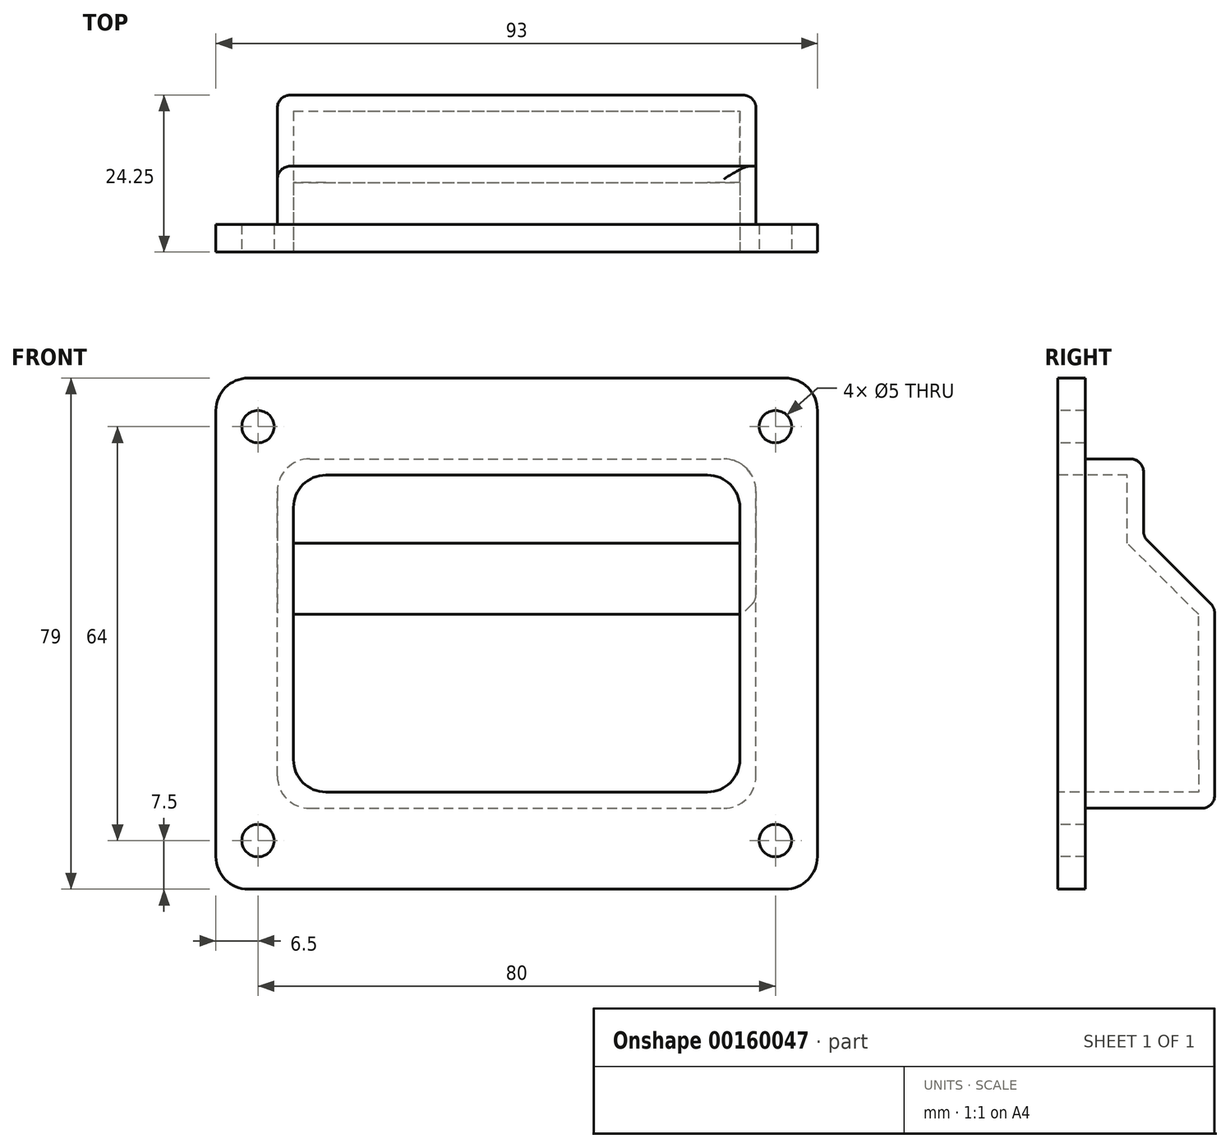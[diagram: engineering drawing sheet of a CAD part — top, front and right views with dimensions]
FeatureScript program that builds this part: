
annotation { "Feature Type Name" : "Feature", "Feature Type Description" : "" }
export const myFeature = defineFeature(function(context is Context, id is Id, definition is map)
    precondition{}
    {
        {
            var Q0;
            Q0=qCreatedBy(makeId("Front.planeOp"),FACE);
            var sketch = newSketch(context, id + "F0", { "sketchPlane" : qUnion([Q0])});
            skLineSegment(sketch, "E0.bottom", {"start": v(46.5, -39.5) * mm, "end": v(-46.5, -39.5) * mm});
            skLineSegment(sketch, "E0.top", {"start": v(46.5, 39.5) * mm, "end": v(-46.5, 39.5) * mm});
            skLineSegment(sketch, "E0.left", {"start": v(46.5, -39.5) * mm, "end": v(46.5, 39.5) * mm});
            skLineSegment(sketch, "E0.right", {"start": v(-46.5, -39.5) * mm, "end": v(-46.5, 39.5) * mm});
            skPoint(sketch, "E0.middle", {"position": v(0, 0) * mm});
            skLineSegment(sketch, "E1.bottom", {"start": v(34.5, -24.5) * mm, "end": v(-34.5, -24.5) * mm});
            skLineSegment(sketch, "E1.top", {"start": v(34.5, 24.5) * mm, "end": v(-34.5, 24.5) * mm});
            skLineSegment(sketch, "E1.left", {"start": v(34.5, -24.5) * mm, "end": v(34.5, 24.5) * mm});
            skLineSegment(sketch, "E1.right", {"start": v(-34.5, -24.5) * mm, "end": v(-34.5, 24.5) * mm});
            skCircle(sketch, "E2", {"center": v(40, 32) * mm, "radius": 2.5 * mm});
            skCircle(sketch, "E3.MirrorC", {"center": v(40, -32) * mm, "radius": 2.5 * mm});
            skCircle(sketch, "E4.MirrorC", {"center": v(-40, 32) * mm, "radius": 2.5 * mm});
            skCircle(sketch, "E5.MirrorC", {"center": v(-40, -32) * mm, "radius": 2.5 * mm});
            skSolve(sketch);
        }
        {
            var Q0;
            Q0=makeQuery(id+"F0.imprint","IMPRINT",FACE,{"disambiguationData":[TD([[makeQuery(id+"F0.imprint","IMPRINT",EDGE,{"derivedFrom":sQuery(id+"F0.wireOp",EDGE,"E0.bottom")}),-1.0]])]});
            extrude(context, id + "F1", {"entities" : qUnion([Q0]), "oppositeDirection" : true, "depth" : 4.25 * mm});
        }
        {
            var Q0;
            Q0=makeQuery(id+"F1.opExtrude","CAP_FACE",FACE,{"disambiguationData":[OSD([sQuery(id+"F0.wireOp",EDGE,"E0.bottom"),sQuery(id+"F0.wireOp",EDGE,"E0.top"),sQuery(id+"F0.wireOp",EDGE,"E0.left"),sQuery(id+"F0.wireOp",EDGE,"E0.right"),sQuery(id+"F0.wireOp",EDGE,"E1.bottom"),sQuery(id+"F0.wireOp",EDGE,"E1.top"),sQuery(id+"F0.wireOp",EDGE,"E1.left"),sQuery(id+"F0.wireOp",EDGE,"E1.right"),sQuery(id+"F0.wireOp",EDGE,"E2"),sQuery(id+"F0.wireOp",EDGE,"E3.MirrorC"),sQuery(id+"F0.wireOp",EDGE,"E4.MirrorC"),sQuery(id+"F0.wireOp",EDGE,"E5.MirrorC")])],"isStart":false});
            var sketch = newSketch(context, id + "F2", { "sketchPlane" : qUnion([Q0])});
            skLineSegment(sketch, "E6.bottom", {"start": v(37, -27) * mm, "end": v(-37, -27) * mm});
            skLineSegment(sketch, "E6.top", {"start": v(37, 27) * mm, "end": v(-37, 27) * mm});
            skLineSegment(sketch, "E6.left", {"start": v(37, -27) * mm, "end": v(37, 27) * mm});
            skLineSegment(sketch, "E6.right", {"start": v(-37, -27) * mm, "end": v(-37, 27) * mm});
            skPoint(sketch, "E6.middle", {"position": v(0, 0) * mm});
            skLineSegment(sketch, "E7.bottom", {"start": v(34.5, -24.5) * mm, "end": v(-34.5, -24.5) * mm});
            skLineSegment(sketch, "E7.top", {"start": v(34.5, 24.5) * mm, "end": v(-34.5, 24.5) * mm});
            skLineSegment(sketch, "E7.left", {"start": v(34.5, -24.5) * mm, "end": v(34.5, 24.5) * mm});
            skLineSegment(sketch, "E7.right", {"start": v(-34.5, -24.5) * mm, "end": v(-34.5, 24.5) * mm});
            skSolve(sketch);
        }
        {
            var Q0;
            Q0 = qSketchRegion(id + "F2", true);
            extrude(context, id + "F3", {"entities" : qUnion([Q0]), "operationType" : NewBodyOperationType.ADD, "depth" : 20 * mm});
        }
        {
            var Q0;
            Q0=makeQuery(id+"F3.opExtrude","CAP_FACE",FACE,{"disambiguationData":[OSD([sQuery(id+"F2.wireOp",EDGE,"E6.bottom"),sQuery(id+"F2.wireOp",EDGE,"E6.top"),sQuery(id+"F2.wireOp",EDGE,"E6.left"),sQuery(id+"F2.wireOp",EDGE,"E6.right"),sQuery(id+"F2.wireOp",EDGE,"E7.bottom"),sQuery(id+"F2.wireOp",EDGE,"E7.top"),sQuery(id+"F2.wireOp",EDGE,"E7.left"),sQuery(id+"F2.wireOp",EDGE,"E7.right")])],"isStart":false});
            var sketch = newSketch(context, id + "F4", { "sketchPlane" : qUnion([Q0])});
            skLineSegment(sketch, "E8.bottom", {"start": v(37, -27) * mm, "end": v(-37, -27) * mm});
            skLineSegment(sketch, "E8.top", {"start": v(37, 27) * mm, "end": v(-37, 27) * mm});
            skLineSegment(sketch, "E8.left", {"start": v(37, -27) * mm, "end": v(37, 27) * mm});
            skLineSegment(sketch, "E8.right", {"start": v(-37, -27) * mm, "end": v(-37, 27) * mm});
            skPoint(sketch, "E8.middle", {"position": v(0, 0) * mm});
            skSolve(sketch);
        }
        {
            var Q0;
            Q0=makeQuery(id+"F3.opExtrude","SWEPT_FACE",FACE,{"disambiguationData":[OSD([sQuery(id+"F2.wireOp",EDGE,"E6.right")])]});
            var sketch = newSketch(context, id + "F5", { "sketchPlane" : qUnion([Q0])});
            skLineSegment(sketch, "E9", {"start": v(13.25, 29.4) * mm, "end": v(13.25, 15) * mm});
            skLineSegment(sketch, "E10", {"start": v(13.25, 15) * mm, "end": v(24.25, 4) * mm});
            skLineSegment(sketch, "E11", {"start": v(24.25, 4) * mm, "end": v(24.25, 29.4) * mm});
            skLineSegment(sketch, "E12", {"start": v(24.25, 29.4) * mm, "end": v(13.25, 29.4) * mm});
            skSolve(sketch);
        }
        {
            var Q0;
            Q0 = qSketchRegion(id + "F5", true);
            extrude(context, id + "F6", {"entities" : qUnion([Q0]), "operationType" : NewBodyOperationType.REMOVE, "endBound" : BoundingType.THROUGH_ALL, "oppositeDirection" : true, "depth" : 25 * mm});
        }
        {
            var Q0;
            Q0=makeQuery(id+"F3.opExtrude","SWEPT_FACE",FACE,{"disambiguationData":[OSD([sQuery(id+"F2.wireOp",EDGE,"E6.right")])]});
            var sketch = newSketch(context, id + "F7", { "sketchPlane" : qUnion([Q0])});
            skLineSegment(sketch, "E13", {"start": v(10.75, 28) * mm, "end": v(10.75, 13.96) * mm});
            skLineSegment(sketch, "E14", {"start": v(10.75, 13.96) * mm, "end": v(21.75, 2.96) * mm});
            skLineSegment(sketch, "E15", {"start": v(21.75, 2.96) * mm, "end": v(21.75, -27) * mm});
            skSolve(sketch);
        }
        {
            var Q0;
            {var subQ2=sQuery(id+"F7.wireOp",EDGE,"E13");Q0=makeQuery(id+"F7.imprint","IMPRINT",FACE,{"disambiguationData":[TD([[makeQuery(id+"F7.imprint","IMPRINT",EDGE,{"derivedFrom":subQ2}),1.0]])]});}
            var Q1;
            Q1=makeQuery(id+"F3.boolean.opBoolean","MERGE",FACE,{"derivedFrom":[makeQuery(id+"F1.opExtrude","SWEPT_FACE",FACE,{"disambiguationData":[OSD([sQuery(id+"F0.wireOp",EDGE,"E1.right")])]}),makeQuery(id+"F3.opExtrude","SWEPT_FACE",FACE,{"disambiguationData":[OSD([sQuery(id+"F2.wireOp",EDGE,"E7.left")])]})]});
            extrude(context, id + "F8", {"entities" : qUnion([Q0]), "operationType" : NewBodyOperationType.ADD, "endBound" : BoundingType.UP_TO_SURFACE, "oppositeDirection" : true, "endBoundEntityFace" : qUnion([Q1]), "depth" : 25 * mm});
        }
        {
            var Q0;
            Q0=makeQuery(id+"F3.opExtrude","SWEPT_EDGE",EDGE,{"disambiguationData":[OSD([sQuery(id+"F2.wireOp",EDGE,"E6.bottom"),sQuery(id+"F2.wireOp",EDGE,"E6.right")])]});
            var Q1;
            Q1=makeQuery(id+"F3.opExtrude","SWEPT_EDGE",EDGE,{"disambiguationData":[OSD([sQuery(id+"F2.wireOp",EDGE,"E6.top"),sQuery(id+"F2.wireOp",EDGE,"E6.right")])]});
            var Q2;
            Q2=makeQuery(id+"F3.opExtrude","SWEPT_EDGE",EDGE,{"disambiguationData":[OSD([sQuery(id+"F2.wireOp",EDGE,"E6.top"),sQuery(id+"F2.wireOp",EDGE,"E6.left")])]});
            var Q3;
            Q3=makeQuery(id+"F3.opExtrude","SWEPT_EDGE",EDGE,{"disambiguationData":[OSD([sQuery(id+"F2.wireOp",EDGE,"E6.bottom"),sQuery(id+"F2.wireOp",EDGE,"E6.left")])]});
            var Q4;
            Q4=makeQuery(id+"F1.opExtrude","SWEPT_EDGE",EDGE,{"disambiguationData":[OSD([sQuery(id+"F0.wireOp",EDGE,"E0.top"),sQuery(id+"F0.wireOp",EDGE,"E0.right")])]});
            var Q5;
            Q5=makeQuery(id+"F1.opExtrude","SWEPT_EDGE",EDGE,{"disambiguationData":[OSD([sQuery(id+"F0.wireOp",EDGE,"E0.bottom"),sQuery(id+"F0.wireOp",EDGE,"E0.right")])]});
            var Q6;
            Q6=makeQuery(id+"F1.opExtrude","SWEPT_EDGE",EDGE,{"disambiguationData":[OSD([sQuery(id+"F0.wireOp",EDGE,"E0.top"),sQuery(id+"F0.wireOp",EDGE,"E0.left")])]});
            var Q7;
            Q7=makeQuery(id+"F1.opExtrude","SWEPT_EDGE",EDGE,{"disambiguationData":[OSD([sQuery(id+"F0.wireOp",EDGE,"E0.bottom"),sQuery(id+"F0.wireOp",EDGE,"E0.left")])]});
            var Q8;
            Q8=makeQuery(id+"F3.boolean.opBoolean","MERGE",EDGE,{"derivedFrom":[makeQuery(id+"F1.opExtrude","SWEPT_EDGE",EDGE,{"disambiguationData":[OSD([sQuery(id+"F0.wireOp",EDGE,"E1.top"),sQuery(id+"F0.wireOp",EDGE,"E1.right")])]}),makeQuery(id+"F3.opExtrude","SWEPT_EDGE",EDGE,{"disambiguationData":[OSD([sQuery(id+"F2.wireOp",EDGE,"E7.top"),sQuery(id+"F2.wireOp",EDGE,"E7.left")])]})]});
            var Q9;
            Q9=makeQuery(id+"F3.boolean.opBoolean","MERGE",EDGE,{"derivedFrom":[makeQuery(id+"F1.opExtrude","SWEPT_EDGE",EDGE,{"disambiguationData":[OSD([sQuery(id+"F0.wireOp",EDGE,"E1.top"),sQuery(id+"F0.wireOp",EDGE,"E1.left")])]}),makeQuery(id+"F3.opExtrude","SWEPT_EDGE",EDGE,{"disambiguationData":[OSD([sQuery(id+"F2.wireOp",EDGE,"E7.top"),sQuery(id+"F2.wireOp",EDGE,"E7.right")])]})]});
            var Q10;
            Q10=makeQuery(id+"F3.boolean.opBoolean","MERGE",EDGE,{"derivedFrom":[makeQuery(id+"F1.opExtrude","SWEPT_EDGE",EDGE,{"disambiguationData":[OSD([sQuery(id+"F0.wireOp",EDGE,"E1.bottom"),sQuery(id+"F0.wireOp",EDGE,"E1.left")])]}),makeQuery(id+"F3.opExtrude","SWEPT_EDGE",EDGE,{"disambiguationData":[OSD([sQuery(id+"F2.wireOp",EDGE,"E7.bottom"),sQuery(id+"F2.wireOp",EDGE,"E7.right")])]})]});
            var Q11;
            Q11=makeQuery(id+"F3.boolean.opBoolean","MERGE",EDGE,{"derivedFrom":[makeQuery(id+"F1.opExtrude","SWEPT_EDGE",EDGE,{"disambiguationData":[OSD([sQuery(id+"F0.wireOp",EDGE,"E1.bottom"),sQuery(id+"F0.wireOp",EDGE,"E1.right")])]}),makeQuery(id+"F3.opExtrude","SWEPT_EDGE",EDGE,{"disambiguationData":[OSD([sQuery(id+"F2.wireOp",EDGE,"E7.bottom"),sQuery(id+"F2.wireOp",EDGE,"E7.left")])]})]});
            fillet(context, id + "F9", {"entities" : qUnion([Q0, Q1, Q2, Q3, Q4, Q5, Q6, Q7, Q8, Q9, Q10, Q11]), "radius" : 5 * mm, "tangentPropagation" : true, "allowEdgeOverflow" : false});
        }
        {
            var Q0;
            Q0=makeQuery(id+"F6.boolean.opBoolean","COPY",EDGE,{"derivedFrom":makeQuery(id+"F6.opExtrude","CAP_EDGE",EDGE,{"disambiguationData":[OSD([sQuery(id+"F5.wireOp",EDGE,"E9")])],"isStart":true})});
            var Q1;
            Q1=makeQuery(id+"F6.boolean.opBoolean","COPY",EDGE,{"derivedFrom":makeQuery(id+"F6.opExtrude","CAP_EDGE",EDGE,{"disambiguationData":[OSD([sQuery(id+"F5.wireOp",EDGE,"E10")])],"isStart":true})});
            var Q2;
            Q2=makeQuery(id+"F3.opExtrude","CAP_EDGE",EDGE,{"disambiguationData":[OSD([sQuery(id+"F2.wireOp",EDGE,"E6.right")])],"isStart":false});
            var Q3;
            Q3=makeQuery(id+"F6.boolean.opBoolean","INTERSECT",EDGE,{"derivedFrom":[makeQuery(id+"F3.opExtrude","SWEPT_FACE",FACE,{"disambiguationData":[OSD([sQuery(id+"F2.wireOp",EDGE,"E6.left")])]}),makeQuery(id+"F6.opExtrude","SWEPT_FACE",FACE,{"disambiguationData":[OSD([sQuery(id+"F5.wireOp",EDGE,"E10")])]})]});
            var Q4;
            Q4=makeQuery(id+"F6.boolean.opBoolean","INTERSECT",EDGE,{"derivedFrom":[makeQuery(id+"F3.opExtrude","SWEPT_FACE",FACE,{"disambiguationData":[OSD([sQuery(id+"F2.wireOp",EDGE,"E6.top")])]}),makeQuery(id+"F6.opExtrude","SWEPT_FACE",FACE,{"disambiguationData":[OSD([sQuery(id+"F5.wireOp",EDGE,"E9")])]})]});
            var Q5;
            Q5=makeQuery(id+"F3.opExtrude","CAP_EDGE",EDGE,{"disambiguationData":[OSD([sQuery(id+"F2.wireOp",EDGE,"E6.bottom")])],"isStart":false});
            var Q6;
            Q6=makeQuery(id+"F3.opExtrude","CAP_EDGE",EDGE,{"disambiguationData":[OSD([sQuery(id+"F2.wireOp",EDGE,"E6.left")])],"isStart":false});
            var Q7;
            Q7=makeQuery(id+"F6.boolean.opBoolean","INTERSECT",EDGE,{"derivedFrom":[makeQuery(id+"F3.opExtrude","SWEPT_FACE",FACE,{"disambiguationData":[OSD([sQuery(id+"F2.wireOp",EDGE,"E6.left")])]}),makeQuery(id+"F6.opExtrude","SWEPT_FACE",FACE,{"disambiguationData":[OSD([sQuery(id+"F5.wireOp",EDGE,"E9")])]})]});
            var Q8;
            {var subQ0=sQuery(id+"F5.wireOp",EDGE,"E10");var subQ1=sQuery(id+"F2.wireOp",EDGE,"E6.right");var subQ7=makeQuery(id+"F6.opExtrude","SWEPT_EDGE",EDGE,{"disambiguationData":[OSD([subQ1,subQ0,sQuery(id+"F5.wireOp",EDGE,"E11")])]});Q8=makeQuery(id+"F8.boolean.opBoolean","MERGE",EDGE,{"derivedFrom":[makeQuery(id+"F6.boolean.opBoolean","COPY",EDGE,{"disambiguationData":[TD([makeQuery(id+"F1.opExtrude","SWEPT_FACE",FACE,{"disambiguationData":[OSD([sQuery(id+"F0.wireOp",EDGE,"E1.left")])]})])],"derivedFrom":subQ7}),makeQuery(id+"F6.boolean.opBoolean","COPY",EDGE,{"disambiguationData":[TD([makeQuery(id+"F1.opExtrude","SWEPT_FACE",FACE,{"disambiguationData":[OSD([sQuery(id+"F0.wireOp",EDGE,"E1.right")])]})])],"derivedFrom":subQ7}),makeQuery(id+"F8.opExtrude","SWEPT_EDGE",EDGE,{"disambiguationData":[OSD([subQ1,subQ0])]})]});}
            var Q9;
            {var subQ0=sQuery(id+"F5.wireOp",EDGE,"E10");var subQ1=sQuery(id+"F5.wireOp",EDGE,"E9");var subQ4=makeQuery(id+"F6.opExtrude","SWEPT_EDGE",EDGE,{"disambiguationData":[OSD([subQ1,subQ0])]});Q9=makeQuery(id+"F8.boolean.opBoolean","MERGE",EDGE,{"derivedFrom":[makeQuery(id+"F6.boolean.opBoolean","COPY",EDGE,{"disambiguationData":[TD([makeQuery(id+"F1.opExtrude","SWEPT_FACE",FACE,{"disambiguationData":[OSD([sQuery(id+"F0.wireOp",EDGE,"E1.left")])]})])],"derivedFrom":subQ4}),makeQuery(id+"F6.boolean.opBoolean","COPY",EDGE,{"disambiguationData":[TD([makeQuery(id+"F1.opExtrude","SWEPT_FACE",FACE,{"disambiguationData":[OSD([sQuery(id+"F0.wireOp",EDGE,"E1.right")])]})])],"derivedFrom":subQ4}),makeQuery(id+"F8.opExtrude","SWEPT_EDGE",EDGE,{"disambiguationData":[OSD([subQ1,subQ0])]})]});}
            fillet(context, id + "F10", {"entities" : qUnion([Q0, Q1, Q2, Q3, Q4, Q5, Q6, Q7, Q8, Q9]), "radius" : 2 * mm, "allowEdgeOverflow" : false});
        }
    });
